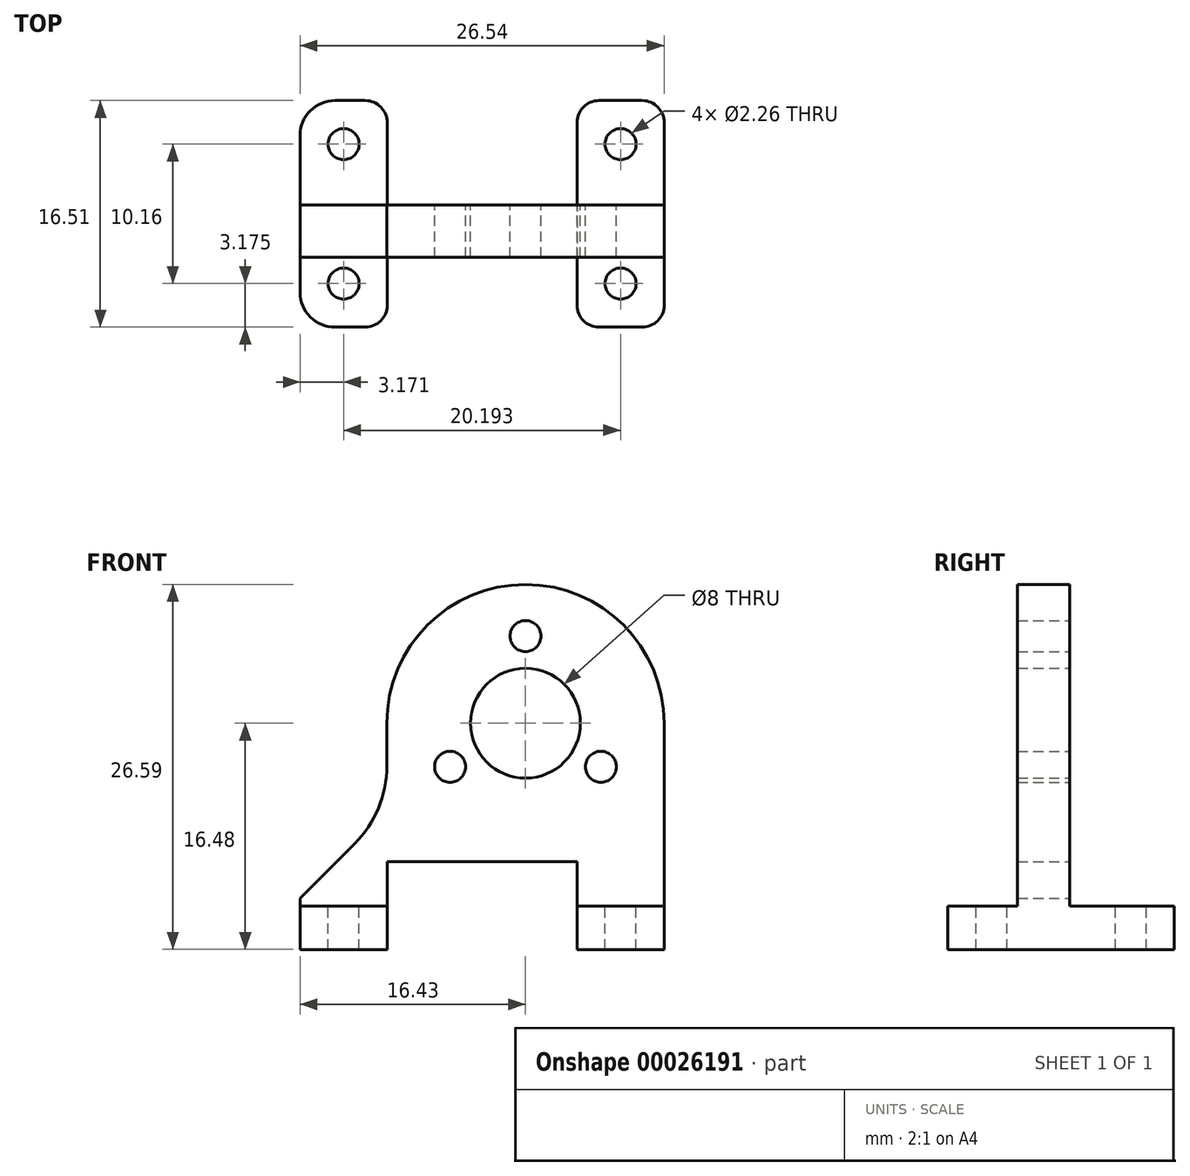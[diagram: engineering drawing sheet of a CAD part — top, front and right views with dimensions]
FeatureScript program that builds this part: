
annotation { "Feature Type Name" : "Feature", "Feature Type Description" : "" }
export const myFeature = defineFeature(function(context is Context, id is Id, definition is map)
    precondition{}
    {
        {
            var Q0;
            Q0=qCreatedBy(makeId("Front.planeOp"),FACE);
            var sketch = newSketch(context, id + "F0", { "sketchPlane" : qUnion([Q0])});
            skArc(sketch, "E0", {"start": v(-0.72, -10.08) * mm, "mid": v(0, -10.1) * mm, "end": v(0.72, -10.08) * mm});
            skLineSegment(sketch, "E1", {"start": v(10.1, 0) * mm, "end": v(10.1, -13.3) * mm});
            skLineSegment(sketch, "E2", {"start": v(10.1, -13.3) * mm, "end": v(3.76, -13.3) * mm});
            skLineSegment(sketch, "E3", {"start": v(3.76, -13.3) * mm, "end": v(3.76, -10.08) * mm});
            skLineSegment(sketch, "E4", {"start": v(3.76, -10.08) * mm, "end": v(-10.08, -10.08) * mm});
            skLineSegment(sketch, "E5", {"start": v(-10.08, -10.08) * mm, "end": v(-10.08, -13.3) * mm});
            skLineSegment(sketch, "E6", {"start": v(-10.08, -13.3) * mm, "end": v(-16.43, -13.3) * mm});
            skLineSegment(sketch, "E7", {"start": v(-10.1, -6.43) * mm, "end": v(-10.1, 0) * mm});
            skLineSegment(sketch, "E8", {"start": v(-16.43, -13.3) * mm, "end": v(-16.43, -12.75) * mm});
            skLineSegment(sketch, "E9", {"start": v(-16.43, -12.75) * mm, "end": v(-10.1, -6.43) * mm});
            skArc(sketch, "E10.trimOffspring", {"start": v(10.1, 0) * mm, "mid": v(0, 10.1) * mm, "end": v(-10.1, 0) * mm});
            skCircle(sketch, "E11", {"center": v(0, 0) * mm, "radius": 4 * mm});
            skLineSegment(sketch, "E12", {"start": v(0, 6.35) * mm, "end": v(-5.5, -3.17) * mm, "construction": true});
            skLineSegment(sketch, "E13", {"start": v(-5.5, -3.17) * mm, "end": v(5.5, -3.17) * mm, "construction": true});
            skLineSegment(sketch, "E14", {"start": v(5.5, -3.17) * mm, "end": v(0, 6.35) * mm, "construction": true});
            skLineSegment(sketch, "E15", {"start": v(0, -3.17) * mm, "end": v(0, -4) * mm, "construction": true});
            skLineSegment(sketch, "E16", {"start": v(2.75, 1.59) * mm, "end": v(3.46, 2) * mm, "construction": true});
            skLineSegment(sketch, "E17", {"start": v(-2.75, 1.59) * mm, "end": v(-3.46, 2) * mm, "construction": true});
            skCircle(sketch, "E18", {"center": v(0, 6.35) * mm, "radius": 1.13 * mm});
            skCircle(sketch, "E19", {"center": v(5.5, -3.17) * mm, "radius": 1.13 * mm});
            skCircle(sketch, "E20", {"center": v(-5.5, -3.17) * mm, "radius": 1.13 * mm});
            skSolve(sketch);
        }
        {
            var Q0;
            Q0=makeQuery(id+"F0.imprint","IMPRINT",FACE,{"disambiguationData":[TD([[makeQuery(id+"F0.imprint","IMPRINT",EDGE,{"derivedFrom":sQuery(id+"F0.wireOp",EDGE,"E1")}),-1.0]])]});
            extrude(context, id + "F1", {"entities" : qUnion([Q0]), "depth" : 3.8 * mm});
        }
        {
            var Q0;
            Q0=makeQuery(id+"F1.opExtrude","SWEPT_EDGE",EDGE,{"disambiguationData":[OSD([sQuery(id+"F0.wireOp",EDGE,"E7"),sQuery(id+"F0.wireOp",EDGE,"E9")])]});
            fillet(context, id + "F2", {"entities" : qUnion([Q0]), "radius" : 8 * mm, "tangentPropagation" : true, "allowEdgeOverflow" : false});
        }
        {
            var Q0;
            Q0=makeQuery(id+"F1.opExtrude","SWEPT_FACE",FACE,{"disambiguationData":[OSD([sQuery(id+"F0.wireOp",EDGE,"E6")])]});
            var sketch = newSketch(context, id + "F3", { "sketchPlane" : qUnion([Q0])});
            skLineSegment(sketch, "E21.bottom", {"start": v(-10.08, -7.62) * mm, "end": v(-16.43, -7.62) * mm});
            skLineSegment(sketch, "E21.top", {"start": v(-10.08, 8.9) * mm, "end": v(-16.43, 8.9) * mm});
            skLineSegment(sketch, "E21.left", {"start": v(-10.08, -7.62) * mm, "end": v(-10.08, 8.9) * mm});
            skLineSegment(sketch, "E21.right", {"start": v(-16.43, -7.62) * mm, "end": v(-16.43, 8.9) * mm});
            skLineSegment(sketch, "E22.bottom", {"start": v(10.1, -7.62) * mm, "end": v(3.76, -7.62) * mm});
            skLineSegment(sketch, "E22.top", {"start": v(10.1, 8.9) * mm, "end": v(3.76, 8.9) * mm});
            skLineSegment(sketch, "E22.left", {"start": v(10.1, -7.62) * mm, "end": v(10.1, 8.9) * mm});
            skLineSegment(sketch, "E22.right", {"start": v(3.76, -7.62) * mm, "end": v(3.76, 8.9) * mm});
            skLineSegment(sketch, "E23", {"start": v(-13.26, 8.9) * mm, "end": v(-13.26, -7.62) * mm, "construction": true});
            skLineSegment(sketch, "E24", {"start": v(6.93, 8.9) * mm, "end": v(6.93, -7.62) * mm, "construction": true});
            skCircle(sketch, "E25", {"center": v(-13.26, 5.72) * mm, "radius": 1.13 * mm});
            skCircle(sketch, "E26", {"center": v(-13.26, -4.44) * mm, "radius": 1.13 * mm});
            skCircle(sketch, "E27", {"center": v(6.93, 5.72) * mm, "radius": 1.13 * mm});
            skCircle(sketch, "E28", {"center": v(6.93, -4.44) * mm, "radius": 1.13 * mm});
            skSolve(sketch);
        }
        {
            var Q0;
            {var subQ2=sQuery(id+"F3.wireOp",EDGE,"E21.top");Q0=makeQuery(id+"F3.imprint","IMPRINT",FACE,{"disambiguationData":[TD([[makeQuery(id+"F3.imprint","IMPRINT",EDGE,{"derivedFrom":subQ2}),1.0]])]});}
            var Q1;
            {var subQ0=sQuery(id+"F0.wireOp",EDGE,"E6");var subQ2=makeQuery(id+"F1.opExtrude","CAP_EDGE",EDGE,{"disambiguationData":[OSD([subQ0])],"isStart":true});Q1=makeQuery(id+"F3.imprint","IMPRINT",FACE,{"disambiguationData":[TD([[makeQuery(id+"F3.imprint","IMPRINT",EDGE,{"derivedFrom":subQ2}),-1.0]])]});}
            var Q2;
            {var subQ2=sQuery(id+"F3.wireOp",EDGE,"E21.bottom");Q2=makeQuery(id+"F3.imprint","IMPRINT",FACE,{"disambiguationData":[TD([[makeQuery(id+"F3.imprint","IMPRINT",EDGE,{"derivedFrom":subQ2}),-1.0]])]});}
            var Q3;
            Q3=makeQuery(id+"F3.imprint","IMPRINT",FACE,{"disambiguationData":[TD([[makeQuery(id+"F3.imprint","IMPRINT",EDGE,{"derivedFrom":sQuery(id+"F3.wireOp",EDGE,"E22.bottom")}),-1.0]])]});
            extrude(context, id + "F4", {"entities" : qUnion([Q0, Q1, Q2, Q3]), "operationType" : NewBodyOperationType.ADD, "depth" : 3.17 * mm});
        }
        {
            var Q0;
            Q0=makeQuery(id+"F4.opExtrude","SWEPT_EDGE",EDGE,{"disambiguationData":[OSD([sQuery(id+"F3.wireOp",EDGE,"E21.top"),sQuery(id+"F3.wireOp",EDGE,"E21.left")])]});
            var Q1;
            Q1=makeQuery(id+"F4.opExtrude","SWEPT_EDGE",EDGE,{"disambiguationData":[OSD([sQuery(id+"F3.wireOp",EDGE,"E22.top"),sQuery(id+"F3.wireOp",EDGE,"E22.right")])]});
            var Q2;
            Q2=makeQuery(id+"F4.opExtrude","SWEPT_EDGE",EDGE,{"disambiguationData":[OSD([sQuery(id+"F3.wireOp",EDGE,"E22.top"),sQuery(id+"F3.wireOp",EDGE,"E22.left")])]});
            var Q3;
            Q3=makeQuery(id+"F4.opExtrude","SWEPT_EDGE",EDGE,{"disambiguationData":[OSD([sQuery(id+"F3.wireOp",EDGE,"E22.bottom"),sQuery(id+"F3.wireOp",EDGE,"E22.left")])]});
            var Q4;
            Q4=makeQuery(id+"F4.opExtrude","SWEPT_EDGE",EDGE,{"disambiguationData":[OSD([sQuery(id+"F3.wireOp",EDGE,"E22.bottom"),sQuery(id+"F3.wireOp",EDGE,"E22.right")])]});
            var Q5;
            Q5=makeQuery(id+"F4.opExtrude","SWEPT_EDGE",EDGE,{"disambiguationData":[OSD([sQuery(id+"F3.wireOp",EDGE,"E21.bottom"),sQuery(id+"F3.wireOp",EDGE,"E21.left")])]});
            fillet(context, id + "F5", {"entities" : qUnion([Q0, Q1, Q2, Q3, Q4, Q5]), "radius" : 1.6 * mm, "tangentPropagation" : true, "allowEdgeOverflow" : false});
        }
        {
            var Q0;
            Q0=makeQuery(id+"F4.opExtrude","SWEPT_EDGE",EDGE,{"disambiguationData":[OSD([sQuery(id+"F3.wireOp",EDGE,"E21.bottom"),sQuery(id+"F3.wireOp",EDGE,"E21.right")])]});
            var Q1;
            Q1=makeQuery(id+"F4.opExtrude","SWEPT_EDGE",EDGE,{"disambiguationData":[OSD([sQuery(id+"F3.wireOp",EDGE,"E21.top"),sQuery(id+"F3.wireOp",EDGE,"E21.right")])]});
            fillet(context, id + "F6", {"entities" : qUnion([Q0, Q1]), "radius" : 2.54 * mm, "tangentPropagation" : true, "allowEdgeOverflow" : false});
        }
    });
